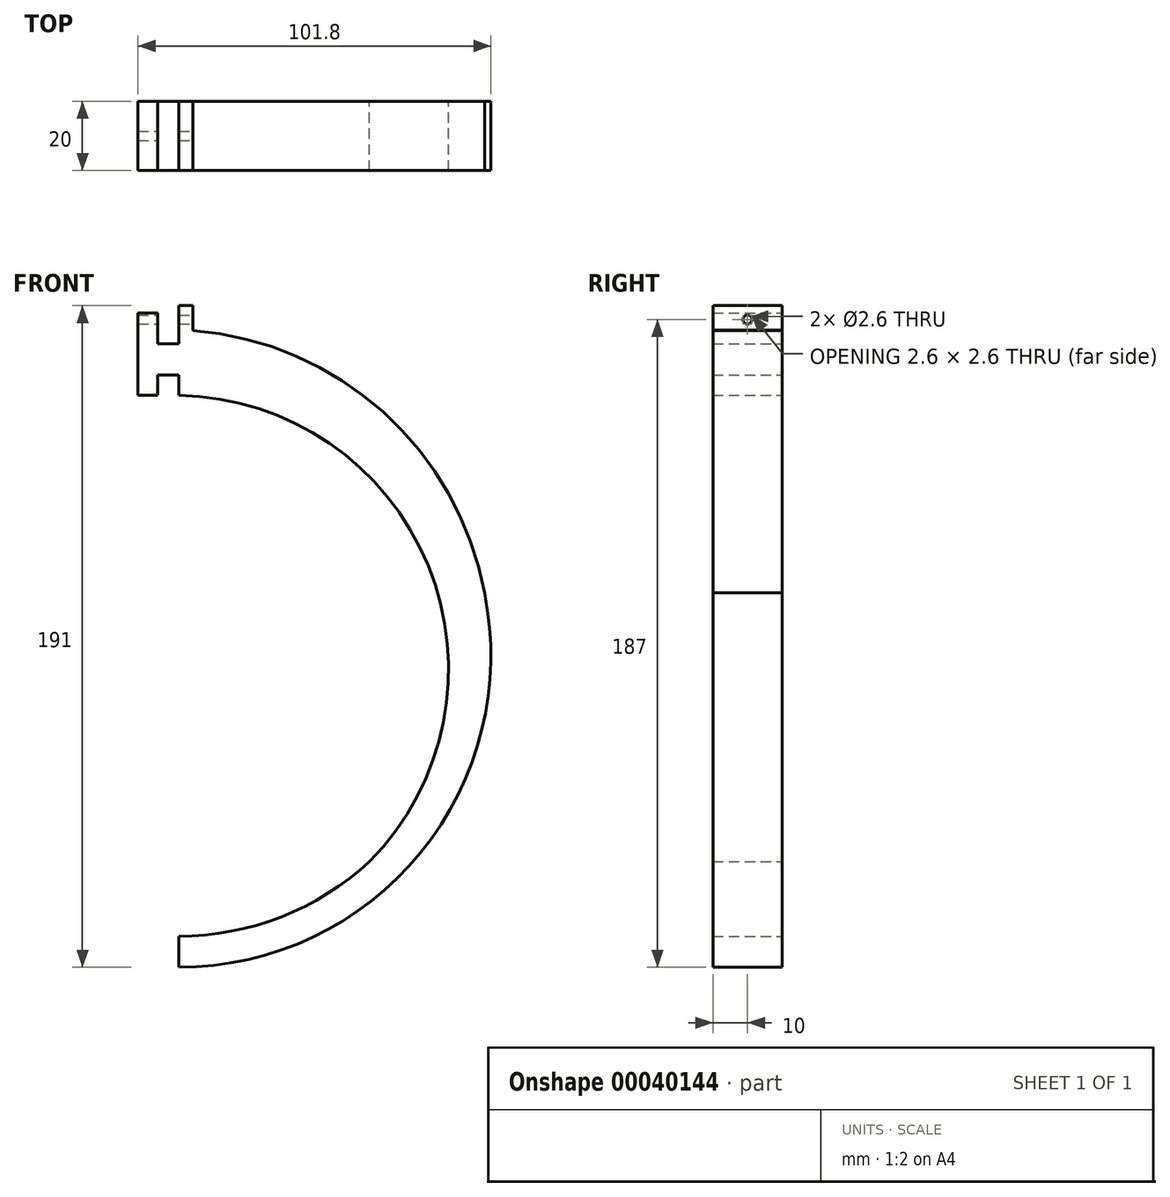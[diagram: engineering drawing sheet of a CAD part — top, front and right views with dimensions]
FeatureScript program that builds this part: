
annotation { "Feature Type Name" : "Feature", "Feature Type Description" : "" }
export const myFeature = defineFeature(function(context is Context, id is Id, definition is map)
    precondition{}
    {
        {
            var Q0;
            Q0=qCreatedBy(makeId("Front.planeOp"),FACE);
            var sketch = newSketch(context, id + "F0", { "sketchPlane" : qUnion([Q0])});
            skArc(sketch, "E0", {"start": v(0, -180) * mm, "mid": v(90, -90) * mm, "end": v(0, 0) * mm});
            skPoint(sketch, "E0.second.point", {"position": v(0, -180) * mm});
            skArc(sketch, "E1.0", {"start": v(0, -171) * mm, "mid": v(81, -90) * mm, "end": v(0, -9) * mm});
            skLineSegment(sketch, "E2", {"start": v(0, -180) * mm, "end": v(0, -171) * mm});
            skLineSegment(sketch, "E3", {"start": v(0, 0) * mm, "end": v(-6.1, 0) * mm});
            skLineSegment(sketch, "E4", {"start": v(-6.1, 0) * mm, "end": v(-6.1, 8.9) * mm});
            skLineSegment(sketch, "E5", {"start": v(-6.1, 8.9) * mm, "end": v(-11.8, 8.9) * mm});
            skLineSegment(sketch, "E6", {"start": v(-11.8, 8.9) * mm, "end": v(-11.8, -14.9) * mm});
            skLineSegment(sketch, "E7", {"start": v(-11.8, -14.9) * mm, "end": v(-6.1, -14.9) * mm});
            skPoint(sketch, "E7.endSnap0", {"position": v(-6.1, 4.45) * mm});
            skLineSegment(sketch, "E8", {"start": v(-6.1, -14.9) * mm, "end": v(-6.1, -9) * mm});
            skLineSegment(sketch, "E9", {"start": v(-6.1, -9) * mm, "end": v(0, -9) * mm});
            skLineSegment(sketch, "E10", {"start": v(0, -9) * mm, "end": v(0, -14.9) * mm});
            skLineSegment(sketch, "E11", {"start": v(0, 0) * mm, "end": v(0, 8.9) * mm});
            skArc(sketch, "E12", {"start": v(54.98, -149.48) * mm, "mid": v(71.91, -64.04) * mm, "end": v(0, -14.9) * mm});
            skLineSegment(sketch, "E13.bottom", {"start": v(0, 8.9) * mm, "end": v(4, 8.9) * mm});
            skLineSegment(sketch, "E13.left", {"start": v(0, 8.9) * mm, "end": v(0, 4.03) * mm});
            skLineSegment(sketch, "E13.right", {"start": v(4, 8.9) * mm, "end": v(4, 4) * mm});
            skArc(sketch, "E14", {"start": v(47.56, -166.4) * mm, "mid": v(86.28, -63.75) * mm, "end": v(0, 4.03) * mm});
            skLineSegment(sketch, "E15.top", {"start": v(0, 11) * mm, "end": v(4, 11) * mm});
            skLineSegment(sketch, "E15.left", {"start": v(0, 8.9) * mm, "end": v(0, 11) * mm});
            skLineSegment(sketch, "E15.right", {"start": v(4, 8.9) * mm, "end": v(4, 11) * mm});
            skLineSegment(sketch, "E16", {"start": v(4, 4) * mm, "end": v(4, 3.81) * mm});
            skLineSegment(sketch, "E17", {"start": v(4, 3.81) * mm, "end": v(4, 3.81) * mm});
            skSolve(sketch);
        }
        {
            var Q0;
            Q0 = qSketchRegion(id + "F0", true);
            extrude(context, id + "F1", {"entities" : qUnion([Q0]), "depth" : 20 * mm});
        }
        {
            var Q0;
            Q0=makeQuery(id+"F1.opExtrude","SWEPT_FACE",FACE,{"disambiguationData":[OSD([sQuery(id+"F0.wireOp",EDGE,"E13.right"),sQuery(id+"F0.wireOp",EDGE,"rNGeiCxC-A0cX-1Tvg-C4XU-t9c1H6emfZL1")])]});
            var sketch = newSketch(context, id + "F2", { "sketchPlane" : qUnion([Q0])});
            skCircle(sketch, "E18", {"center": v(-10, 7) * mm, "radius": 1.3 * mm});
            skSolve(sketch);
        }
        {
            var Q0;
            Q0 = qSketchRegion(id + "F2", true);
            extrude(context, id + "F3", {"entities" : qUnion([Q0]), "operationType" : NewBodyOperationType.REMOVE, "oppositeDirection" : true, "depth" : 25 * mm});
        }
    });
